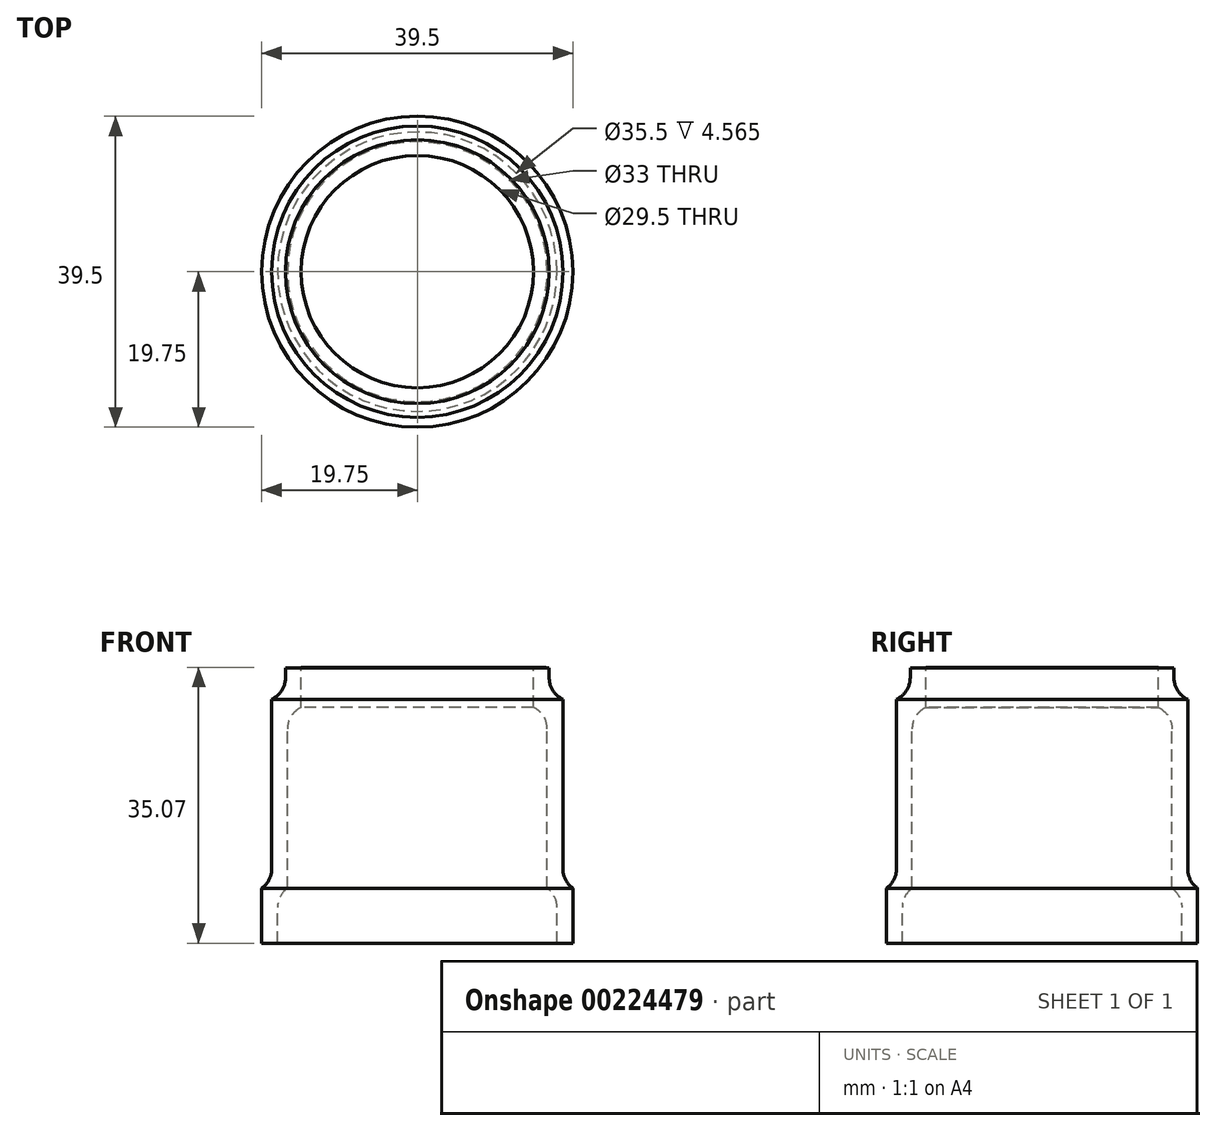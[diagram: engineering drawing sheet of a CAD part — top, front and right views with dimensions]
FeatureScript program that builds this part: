
annotation { "Feature Type Name" : "Feature", "Feature Type Description" : "" }
export const myFeature = defineFeature(function(context is Context, id is Id, definition is map)
    precondition{}
    {
        {
            var Q0;
            Q0=qCreatedBy(makeId("Front.planeOp"),FACE);
            var sketch = newSketch(context, id + "F0", { "sketchPlane" : qUnion([Q0])});
            skLineSegment(sketch, "E0", {"start": v(0, 57.48) * mm, "end": v(0, -59.82) * mm, "construction": true});
            skLineSegment(sketch, "E1", {"start": v(-16.5, 5.74) * mm, "end": v(-14.75, 5.74) * mm});
            skLineSegment(sketch, "E2", {"start": v(-14.75, 5.74) * mm, "end": v(-14.75, 10.84) * mm});
            skLineSegment(sketch, "E3", {"start": v(-17.75, -17.23) * mm, "end": v(-17.75, -24.23) * mm});
            skLineSegment(sketch, "E4.0", {"start": v(-16.75, 6.77) * mm, "end": v(-16.75, 10.77) * mm});
            skLineSegment(sketch, "E5.0", {"start": v(-18.5, -17.23) * mm, "end": v(-18.5, 6.77) * mm});
            skLineSegment(sketch, "E6.0", {"start": v(-19.75, -17.23) * mm, "end": v(-19.75, -24.23) * mm});
            skLineSegment(sketch, "E7", {"start": v(-17.75, -24.23) * mm, "end": v(-19.75, -24.23) * mm});
            skLineSegment(sketch, "E8", {"start": v(-18.5, -17.23) * mm, "end": v(-19.75, -17.23) * mm});
            skLineSegment(sketch, "E9", {"start": v(-18.5, 6.77) * mm, "end": v(-16.75, 6.77) * mm});
            skLineSegment(sketch, "E10", {"start": v(-16.75, 10.77) * mm, "end": v(-14.75, 10.84) * mm});
            skLineSegment(sketch, "E11", {"start": v(-16.5, 5.74) * mm, "end": v(-16.5, 0) * mm});
            skLineSegment(sketch, "E12", {"start": v(-16.5, 0) * mm, "end": v(-16.5, -17.23) * mm});
            skLineSegment(sketch, "E13", {"start": v(-16.5, -17.23) * mm, "end": v(-17.75, -17.23) * mm});
            skSolve(sketch);
        }
        {
            var Q0;
            Q0=makeQuery(id+"F0.imprint","IMPRINT",FACE,{"disambiguationData":[TD([[makeQuery(id+"F0.imprint","IMPRINT",EDGE,{"derivedFrom":sQuery(id+"F0.wireOp",EDGE,"E1")}),1.0]])]});
            var Q1;
            Q1=sQuery(id+"F0.wireOp",EDGE,"E0");
            revolve(context, id + "F1", {"entities" : qUnion([Q0]), "axis" : qUnion([Q1]), "revolveType" : RevolveType.FULL});
        }
        {
            var Q0;
            Q0=makeQuery(id+"F1.opRevolve","SWEPT_EDGE",EDGE,{"disambiguationData":[OSD([sQuery(id+"F0.wireOp",EDGE,"E4.0"),sQuery(id+"F0.wireOp",EDGE,"E9")])]});
            var Q1;
            Q1=makeQuery(id+"F1.opRevolve","SWEPT_EDGE",EDGE,{"disambiguationData":[OSD([sQuery(id+"F0.wireOp",EDGE,"E5.0"),sQuery(id+"F0.wireOp",EDGE,"E8")])]});
            var Q2;
            Q2=makeQuery(id+"F1.opRevolve","SWEPT_EDGE",EDGE,{"disambiguationData":[OSD([sQuery(id+"F0.wireOp",EDGE,"E3"),sQuery(id+"F0.wireOp",EDGE,"E13")])]});
            var Q3;
            Q3=makeQuery(id+"F1.opRevolve","SWEPT_EDGE",EDGE,{"disambiguationData":[OSD([sQuery(id+"F0.wireOp",EDGE,"E1"),sQuery(id+"F0.wireOp",EDGE,"E11")])]});
            fillet(context, id + "F2", {"entities" : qUnion([Q0, Q1, Q2, Q3]), "radius" : 3 * mm, "tangentPropagation" : true, "allowEdgeOverflow" : false});
        }
    });
